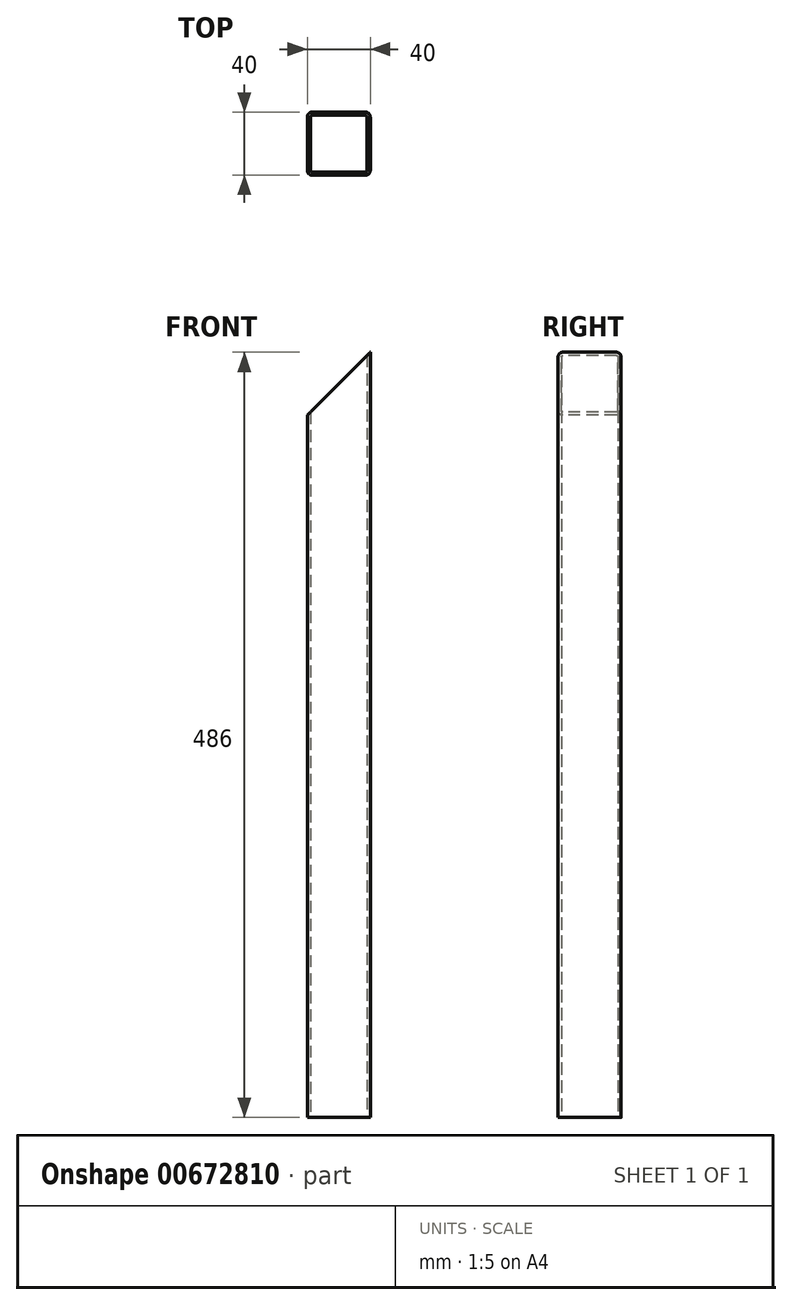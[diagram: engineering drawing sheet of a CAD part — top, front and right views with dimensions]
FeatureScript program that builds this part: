
annotation { "Feature Type Name" : "Feature", "Feature Type Description" : "" }
export const myFeature = defineFeature(function(context is Context, id is Id, definition is map)
    precondition{}
    {
        {
            var Q0;
            Q0=qCreatedBy(makeId("Top.planeOp"),FACE);
            var sketch = newSketch(context, id + "F0", { "sketchPlane" : qUnion([Q0])});
            skLineSegment(sketch, "E0.bottom", {"start": v(-17, 20) * mm, "end": v(17, 20) * mm});
            skLineSegment(sketch, "E0.top", {"start": v(-17, -20) * mm, "end": v(17, -20) * mm});
            skLineSegment(sketch, "E0.left", {"start": v(-20, 17) * mm, "end": v(-20, -17) * mm});
            skLineSegment(sketch, "E0.right", {"start": v(20, 17) * mm, "end": v(20, -17) * mm});
            skPoint(sketch, "E0.middle", {"position": v(0, 0) * mm});
            skPoint(sketch, "E1.visualSharp", {"position": v(-20, 20) * mm});
            skArc(sketch, "E1.filletArc", {"start": v(-17, 20) * mm, "mid": v(-19.12, 19.12) * mm, "end": v(-20, 17) * mm});
            skPoint(sketch, "E2.visualSharp", {"position": v(20, 20) * mm});
            skArc(sketch, "E2.filletArc", {"start": v(20, 17) * mm, "mid": v(19.12, 19.12) * mm, "end": v(17, 20) * mm});
            skPoint(sketch, "E3.visualSharp", {"position": v(20, -20) * mm});
            skArc(sketch, "E3.filletArc", {"start": v(17, -20) * mm, "mid": v(19.12, -19.12) * mm, "end": v(20, -17) * mm});
            skPoint(sketch, "E4.visualSharp", {"position": v(-20, -20) * mm});
            skArc(sketch, "E4.filletArc", {"start": v(-20, -17) * mm, "mid": v(-19.12, -19.12) * mm, "end": v(-17, -20) * mm});
            skArc(sketch, "E5.0", {"start": v(-17, 18) * mm, "mid": v(-17.7, 17.7) * mm, "end": v(-18, 17) * mm});
            skLineSegment(sketch, "E5.1", {"start": v(-18, 17) * mm, "end": v(-18, -17) * mm});
            skLineSegment(sketch, "E5.2", {"start": v(-17, 18) * mm, "end": v(17, 18) * mm});
            skArc(sketch, "E5.3", {"start": v(-18, -17) * mm, "mid": v(-17.7, -17.7) * mm, "end": v(-17, -18) * mm});
            skArc(sketch, "E5.4", {"start": v(18, 17) * mm, "mid": v(17.7, 17.7) * mm, "end": v(17, 18) * mm});
            skLineSegment(sketch, "E5.5", {"start": v(18, 17) * mm, "end": v(18, -17) * mm});
            skArc(sketch, "E5.6", {"start": v(17, -18) * mm, "mid": v(17.7, -17.7) * mm, "end": v(18, -17) * mm});
            skLineSegment(sketch, "E5.7", {"start": v(-17, -18) * mm, "end": v(17, -18) * mm});
            skSolve(sketch);
        }
        {
            var Q0;
            Q0=makeQuery(id+"F0.imprint","IMPRINT",FACE,{"disambiguationData":[TD([[makeQuery(id+"F0.imprint","IMPRINT",EDGE,{"derivedFrom":sQuery(id+"F0.wireOp",EDGE,"E0.bottom")}),-1.0]])]});
            extrude(context, id + "F1", {"entities" : qUnion([Q0]), "endBound" : BoundingType.SYMMETRIC, "depth" : (500 - 14) * mm, "offsetDistance" : 25 * mm});
        }
        {
            var Q0;
            Q0=qCreatedBy(makeId("Front.planeOp"),FACE);
            var sketch = newSketch(context, id + "F2", { "sketchPlane" : qUnion([Q0])});
            skLineSegment(sketch, "E6.0", {"start": v(-20, 243) * mm, "end": v(-20, 203) * mm});
            skLineSegment(sketch, "E7.0", {"start": v(-20, 243) * mm, "end": v(20, 243) * mm});
            skPoint(sketch, "E8.orphan", {"position": v(-17, 243) * mm});
            skLineSegment(sketch, "E9.0", {"start": v(20, 243) * mm, "end": v(20, -243) * mm});
            skPoint(sketch, "E10.orphan", {"position": v(17, 243) * mm});
            skLineSegment(sketch, "E11", {"start": v(20, 243) * mm, "end": v(-20, 203) * mm});
            skPoint(sketch, "E12.orphan", {"position": v(-20, -243) * mm});
            skSolve(sketch);
        }
        {
            var Q0;
            Q0=makeQuery(id+"F2.imprint","IMPRINT",FACE,{"disambiguationData":[TD([[makeQuery(id+"F2.imprint","IMPRINT",EDGE,{"derivedFrom":sQuery(id+"F2.wireOp",EDGE,"E6.0")}),1.0]])]});
            extrude(context, id + "F3", {"entities" : qUnion([Q0]), "operationType" : NewBodyOperationType.REMOVE, "endBound" : BoundingType.THROUGH_ALL, "oppositeDirection" : true, "depth" : 25 * mm, "offsetDistance" : 25 * mm, "hasSecondDirection" : true, "secondDirectionBound" : SecondDirectionBoundingType.THROUGH_ALL, "secondDirectionOppositeDirection" : false, "secondDirectionDepth" : 25 * mm});
        }
    });
